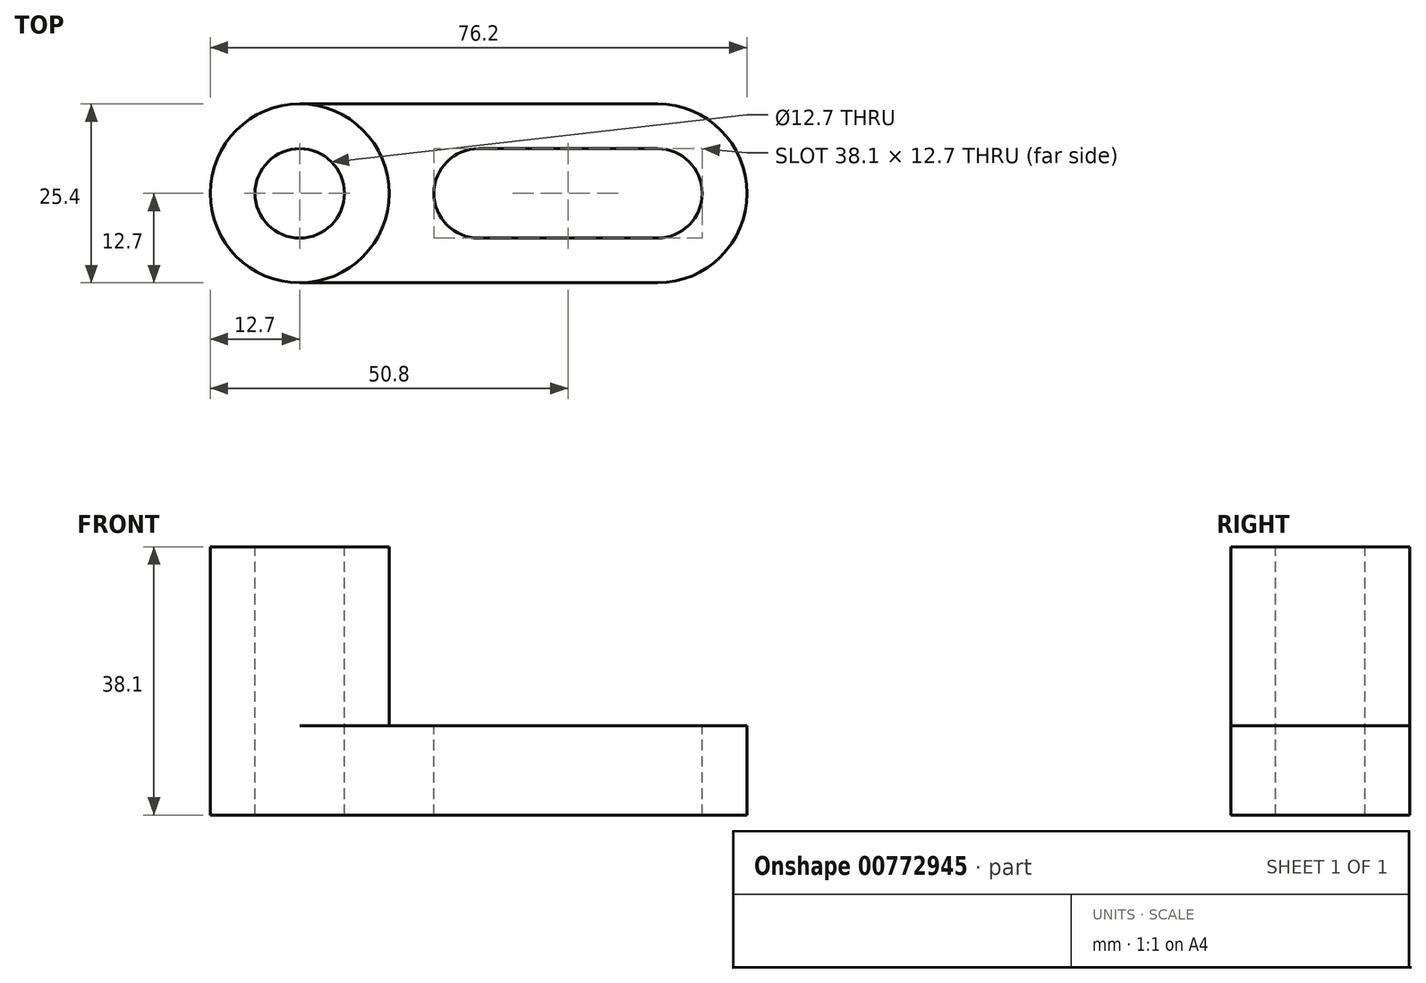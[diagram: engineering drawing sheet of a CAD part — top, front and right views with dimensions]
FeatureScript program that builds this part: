
annotation { "Feature Type Name" : "Feature", "Feature Type Description" : "" }
export const myFeature = defineFeature(function(context is Context, id is Id, definition is map)
    precondition{}
    {
        {
            var Q0;
            Q0=qCreatedBy(makeId("Front.planeOp"),FACE);
            var sketch = newSketch(context, id + "F0", { "sketchPlane" : qUnion([Q0])});
            skLineSegment(sketch, "E0", {"start": v(0, 0) * mm, "end": v(76.2, 0) * mm});
            skLineSegment(sketch, "E1", {"start": v(76.2, 0) * mm, "end": v(76.2, 38.1) * mm});
            skLineSegment(sketch, "E2", {"start": v(76.2, 38.1) * mm, "end": v(0, 38.1) * mm});
            skLineSegment(sketch, "E3", {"start": v(0, 38.1) * mm, "end": v(0, 0) * mm});
            skSolve(sketch);
        }
        {
            var Q0;
            Q0=makeQuery(id+"F0.imprint","IMPRINT",FACE,{"disambiguationData":[TD([[makeQuery(id+"F0.imprint","IMPRINT",EDGE,{"derivedFrom":sQuery(id+"F0.wireOp",EDGE,"E0")}),1.0]])]});
            extrude(context, id + "F1", {"entities" : qUnion([Q0]), "depth" : 25.4 * mm, "offsetDistance" : 25.4 * mm});
        }
        {
            var Q0;
            Q0=makeQuery(id+"F1.opExtrude","SWEPT_FACE",FACE,{"disambiguationData":[OSD([sQuery(id+"F0.wireOp",EDGE,"E2")])]});
            var sketch = newSketch(context, id + "F2", { "sketchPlane" : qUnion([Q0])});
            skCircle(sketch, "E4", {"center": v(12.7, -12.7) * mm, "radius": 12.7 * mm});
            skPoint(sketch, "E4.centerSnap0", {"position": v(0, -12.7) * mm});
            skCircle(sketch, "E5", {"center": v(12.7, -12.7) * mm, "radius": 6.35 * mm});
            skSolve(sketch);
        }
        {
            var Q0;
            {var subQ0=sQuery(id+"F2.wireOp",EDGE,"E4");var subQ1=sQuery(id+"F0.wireOp",EDGE,"E2");var subQ4=makeQuery(id+"F1.opExtrude","CAP_EDGE",EDGE,{"disambiguationData":[OSD([subQ1])],"isStart":true});var subQ5=makeQuery(id+"F2.imprint","INTERSECT",VERTEX,{"derivedFrom":[subQ4,subQ0]});Q0=makeQuery(id+"F2.imprint","IMPRINT",FACE,{"disambiguationData":[TD([[makeQuery(id+"F2.imprint","IMPRINT",EDGE,{"disambiguationData":[TD([[subQ5,-1.0]])],"derivedFrom":subQ0}),-1.0]])]});}
            var Q1;
            {var subQ0=sQuery(id+"F2.wireOp",EDGE,"E4");var subQ1=sQuery(id+"F0.wireOp",EDGE,"E2");var subQ4=makeQuery(id+"F1.opExtrude","CAP_EDGE",EDGE,{"disambiguationData":[OSD([subQ1])],"isStart":false});var subQ5=makeQuery(id+"F2.imprint","INTERSECT",VERTEX,{"derivedFrom":[subQ4,subQ0]});Q1=makeQuery(id+"F2.imprint","IMPRINT",FACE,{"disambiguationData":[TD([[makeQuery(id+"F2.imprint","IMPRINT",EDGE,{"disambiguationData":[TD([[subQ5,1.0]])],"derivedFrom":subQ0}),-1.0]])]});}
            var Q2;
            Q2=makeQuery(id+"F2.imprint","IMPRINT",FACE,{"disambiguationData":[TD([[makeQuery(id+"F2.imprint","IMPRINT",EDGE,{"derivedFrom":sQuery(id+"F2.wireOp",EDGE,"E5")}),1.0]])]});
            var Q3;
            {var subQ1=sQuery(id+"F0.wireOp",EDGE,"E2");var subQ6=makeQuery(id+"F1.opExtrude","SWEPT_EDGE",EDGE,{"disambiguationData":[OSD([sQuery(id+"F0.wireOp",EDGE,"E1"),subQ1])]});Q3=makeQuery(id+"F2.imprint","IMPRINT",FACE,{"disambiguationData":[TD([[makeQuery(id+"F2.imprint","IMPRINT",EDGE,{"derivedFrom":subQ6}),1.0]])]});}
            extrude(context, id + "F3", {"entities" : qUnion([Q0, Q1, Q2, Q3]), "operationType" : NewBodyOperationType.REMOVE, "oppositeDirection" : true, "depth" : 25.4 * mm, "offsetDistance" : 25.4 * mm});
        }
        {
            var Q0;
            {var subQ0=sQuery(id+"F0.wireOp",EDGE,"E2");var subQ1=makeQuery(id+"F1.opExtrude","CAP_EDGE",EDGE,{"disambiguationData":[OSD([subQ0])],"isStart":true});var subQ2=sQuery(id+"F0.wireOp",EDGE,"E3");var subQ3=makeQuery(id+"F1.opExtrude","SWEPT_EDGE",EDGE,{"disambiguationData":[OSD([subQ0,subQ2])]});var subQ4=makeQuery(id+"F2.imprint","INTERSECT",VERTEX,{"derivedFrom":[subQ3,subQ1]});var subQ5=sQuery(id+"F2.wireOp",EDGE,"E4");var subQ6=makeQuery(id+"F2.imprint","INTERSECT",VERTEX,{"derivedFrom":[subQ1,subQ5]});Q0=makeQuery(id+"F3.boolean.opBoolean","COPY",FACE,{"derivedFrom":makeQuery(id+"F3.opExtrude","CAP_FACE",FACE,{"disambiguationData":[OSD([subQ0,subQ2,subQ5]),TDD([makeQuery(id+"F2.imprint","IMPRINT",EDGE,{"disambiguationData":[TD([[subQ6,-1.0]])],"derivedFrom":subQ5}),makeQuery(id+"F2.imprint","IMPRINT",EDGE,{"disambiguationData":[TD([[subQ4,1.0]])],"derivedFrom":subQ3}),makeQuery(id+"F2.imprint","IMPRINT",EDGE,{"disambiguationData":[TD([[subQ6,-1.0]])],"derivedFrom":subQ1})])],"isStart":false})});}
            var Q1;
            {var subQ0=sQuery(id+"F0.wireOp",EDGE,"E2");var subQ1=makeQuery(id+"F1.opExtrude","CAP_EDGE",EDGE,{"disambiguationData":[OSD([subQ0])],"isStart":false});var subQ2=sQuery(id+"F0.wireOp",EDGE,"E3");var subQ3=makeQuery(id+"F1.opExtrude","SWEPT_EDGE",EDGE,{"disambiguationData":[OSD([subQ0,subQ2])]});var subQ4=makeQuery(id+"F2.imprint","INTERSECT",VERTEX,{"derivedFrom":[subQ3,subQ1]});var subQ5=sQuery(id+"F2.wireOp",EDGE,"E4");var subQ6=makeQuery(id+"F2.imprint","INTERSECT",VERTEX,{"derivedFrom":[subQ1,subQ5]});Q1=makeQuery(id+"F3.boolean.opBoolean","COPY",FACE,{"derivedFrom":makeQuery(id+"F3.opExtrude","CAP_FACE",FACE,{"disambiguationData":[OSD([subQ0,subQ2,subQ5]),TDD([makeQuery(id+"F2.imprint","IMPRINT",EDGE,{"disambiguationData":[TD([[subQ6,1.0]])],"derivedFrom":subQ5}),makeQuery(id+"F2.imprint","IMPRINT",EDGE,{"disambiguationData":[TD([[subQ4,-1.0]])],"derivedFrom":subQ3}),makeQuery(id+"F2.imprint","IMPRINT",EDGE,{"disambiguationData":[TD([[subQ6,-1.0]])],"derivedFrom":subQ1})])],"isStart":false})});}
            var Q2;
            Q2=makeQuery(id+"F3.boolean.opBoolean","COPY",FACE,{"derivedFrom":makeQuery(id+"F3.opExtrude","CAP_FACE",FACE,{"disambiguationData":[OSD([sQuery(id+"F2.wireOp",EDGE,"E5")])],"isStart":false})});
            extrude(context, id + "F4", {"entities" : qUnion([Q0, Q1, Q2]), "operationType" : NewBodyOperationType.REMOVE, "oppositeDirection" : true, "depth" : 25.4 * mm, "offsetDistance" : 25.4 * mm});
        }
        {
            var Q0;
            Q0=makeQuery(id+"F3.boolean.opBoolean","COPY",FACE,{"derivedFrom":makeQuery(id+"F3.opExtrude","CAP_FACE",FACE,{"disambiguationData":[OSD([sQuery(id+"F0.wireOp",EDGE,"E1"),sQuery(id+"F0.wireOp",EDGE,"E2"),sQuery(id+"F2.wireOp",EDGE,"E4")])],"isStart":false})});
            var sketch = newSketch(context, id + "F5", { "sketchPlane" : qUnion([Q0])});
            skArc(sketch, "E6", {"start": v(63.5, -25.4) * mm, "mid": v(76.2, -12.7) * mm, "end": v(63.5, 0) * mm});
            skSolve(sketch);
        }
        {
            var Q0;
            {var subQ0=sQuery(id+"F5.wireOp",EDGE,"E6");var subQ1=sQuery(id+"F0.wireOp",EDGE,"E2");var subQ3=sQuery(id+"F0.wireOp",EDGE,"E1");var subQ6=makeQuery(id+"F3.boolean.opBoolean","COPY",EDGE,{"derivedFrom":makeQuery(id+"F3.opExtrude","CAP_EDGE",EDGE,{"disambiguationData":[OSD([subQ3,subQ1])],"isStart":false})});var subQ7=makeQuery(id+"F5.imprint","INTERSECT",VERTEX,{"derivedFrom":[subQ6,subQ0]});Q0=makeQuery(id+"F5.imprint","IMPRINT",FACE,{"disambiguationData":[TD([[makeQuery(id+"F5.imprint","IMPRINT",EDGE,{"disambiguationData":[TD([[subQ7,-1.0]])],"derivedFrom":subQ0}),-1.0]])]});}
            var Q1;
            {var subQ0=sQuery(id+"F5.wireOp",EDGE,"E6");var subQ1=sQuery(id+"F0.wireOp",EDGE,"E2");var subQ3=sQuery(id+"F0.wireOp",EDGE,"E1");var subQ6=makeQuery(id+"F3.boolean.opBoolean","COPY",EDGE,{"derivedFrom":makeQuery(id+"F3.opExtrude","CAP_EDGE",EDGE,{"disambiguationData":[OSD([subQ3,subQ1])],"isStart":false})});var subQ7=makeQuery(id+"F5.imprint","INTERSECT",VERTEX,{"derivedFrom":[subQ6,subQ0]});Q1=makeQuery(id+"F5.imprint","IMPRINT",FACE,{"disambiguationData":[TD([[makeQuery(id+"F5.imprint","IMPRINT",EDGE,{"disambiguationData":[TD([[subQ7,1.0]])],"derivedFrom":subQ0}),-1.0]])]});}
            extrude(context, id + "F6", {"entities" : qUnion([Q0, Q1]), "operationType" : NewBodyOperationType.REMOVE, "oppositeDirection" : true, "depth" : 25.4 * mm, "offsetDistance" : 25.4 * mm});
        }
        {
            var Q0;
            Q0=makeQuery(id+"F3.boolean.opBoolean","COPY",FACE,{"derivedFrom":makeQuery(id+"F3.opExtrude","CAP_FACE",FACE,{"disambiguationData":[OSD([sQuery(id+"F0.wireOp",EDGE,"E1"),sQuery(id+"F0.wireOp",EDGE,"E2"),sQuery(id+"F2.wireOp",EDGE,"E4")])],"isStart":false})});
            var sketch = newSketch(context, id + "F7", { "sketchPlane" : qUnion([Q0])});
            skCircle(sketch, "E7", {"center": v(38.1, -12.7) * mm, "radius": 6.35 * mm});
            skCircle(sketch, "E8", {"center": v(63.5, -12.7) * mm, "radius": 6.35 * mm});
            skLineSegment(sketch, "E9", {"start": v(38.1, -19.05) * mm, "end": v(63.5, -19.05) * mm});
            skLineSegment(sketch, "E10", {"start": v(38.1, -6.35) * mm, "end": v(63.5, -6.35) * mm});
            skSolve(sketch);
        }
        {
            var Q0;
            {var subQ0=sQuery(id+"F7.wireOp",EDGE,"E7");var subQ1=makeQuery(id+"F7.imprint","INTERSECT",VERTEX,{"derivedFrom":[subQ0,sQuery(id+"F7.wireOp",EDGE,"E9")]});Q0=makeQuery(id+"F7.imprint","IMPRINT",FACE,{"disambiguationData":[TD([[makeQuery(id+"F7.imprint","IMPRINT",EDGE,{"disambiguationData":[TD([[subQ1,1.0]])],"derivedFrom":subQ0}),1.0]])]});}
            var Q1;
            {var subQ0=sQuery(id+"F7.wireOp",EDGE,"E9");Q1=makeQuery(id+"F7.imprint","IMPRINT",FACE,{"disambiguationData":[TD([[makeQuery(id+"F7.imprint","IMPRINT",EDGE,{"derivedFrom":subQ0}),1.0]])]});}
            var Q2;
            {var subQ0=sQuery(id+"F7.wireOp",EDGE,"E8");var subQ1=makeQuery(id+"F7.imprint","INTERSECT",VERTEX,{"derivedFrom":[subQ0,sQuery(id+"F7.wireOp",EDGE,"E9")]});Q2=makeQuery(id+"F7.imprint","IMPRINT",FACE,{"disambiguationData":[TD([[makeQuery(id+"F7.imprint","IMPRINT",EDGE,{"disambiguationData":[TD([[subQ1,1.0]])],"derivedFrom":subQ0}),1.0]])]});}
            extrude(context, id + "F8", {"entities" : qUnion([Q0, Q1, Q2]), "operationType" : NewBodyOperationType.REMOVE, "oppositeDirection" : true, "depth" : 25.4 * mm, "offsetDistance" : 25.4 * mm});
        }
    });
